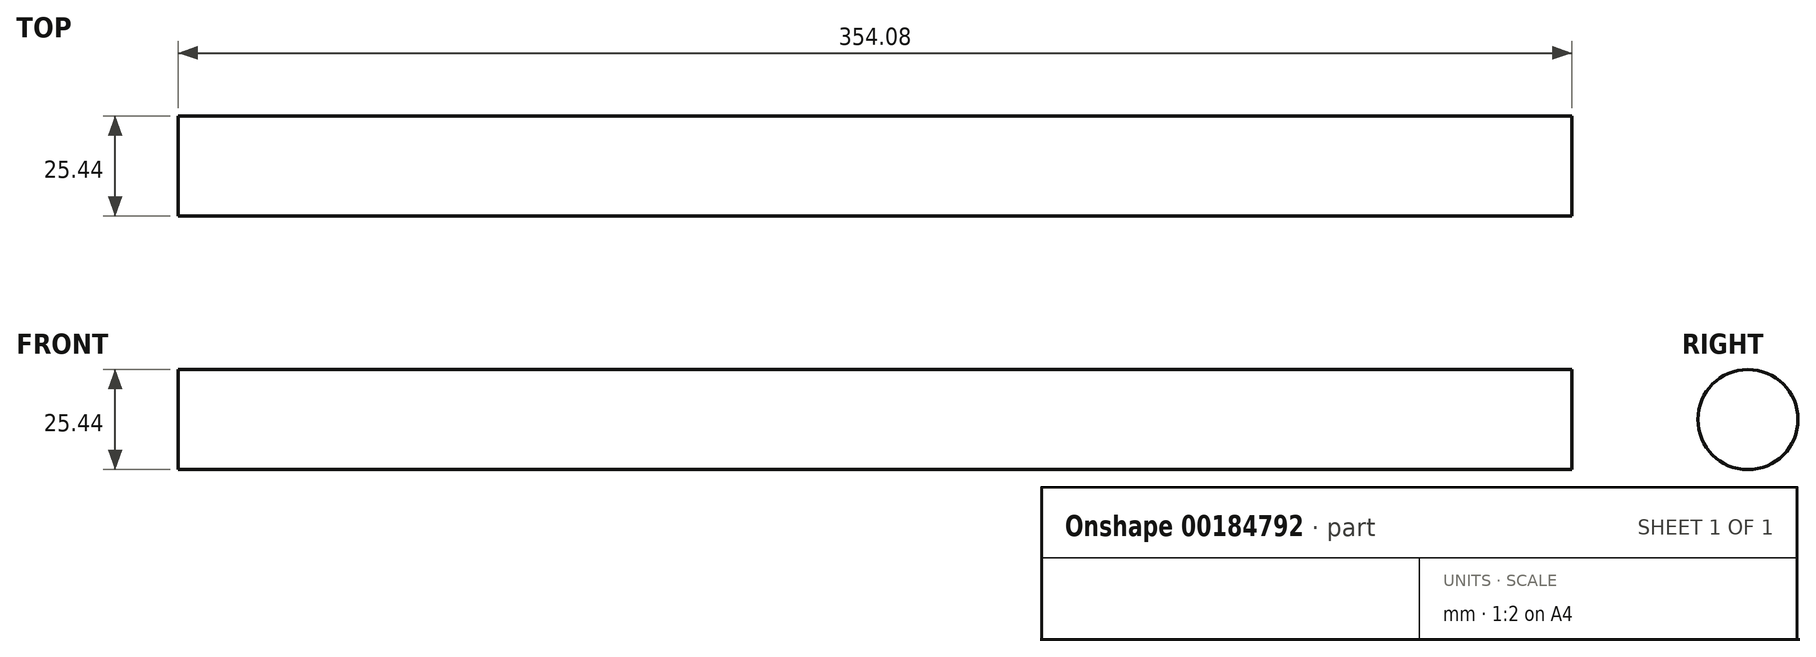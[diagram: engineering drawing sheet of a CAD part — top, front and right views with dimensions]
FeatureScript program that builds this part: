
annotation { "Feature Type Name" : "Feature", "Feature Type Description" : "" }
export const myFeature = defineFeature(function(context is Context, id is Id, definition is map)
    precondition{}
    {
        {
            var Q0;
            Q0=qCreatedBy(makeId("Right.planeOp"),FACE);
            var sketch = newSketch(context, id + "F0", { "sketchPlane" : qUnion([Q0])});
            skCircle(sketch, "E0", {"center": v(0, 0) * mm, "radius": 12.72 * mm});
            skSolve(sketch);
        }
        {
            var Q0;
            Q0=makeQuery(id+"F0.imprint","IMPRINT",FACE,{"disambiguationData":[TD([[makeQuery(id+"F0.imprint","IMPRINT",EDGE,{"derivedFrom":sQuery(id+"F0.wireOp",EDGE,"E0")}),1.0]])]});
            extrude(context, id + "F1", {"entities" : qUnion([Q0]), "endBound" : BoundingType.SYMMETRIC, "depth" : 354.08 * mm});
        }
    });
